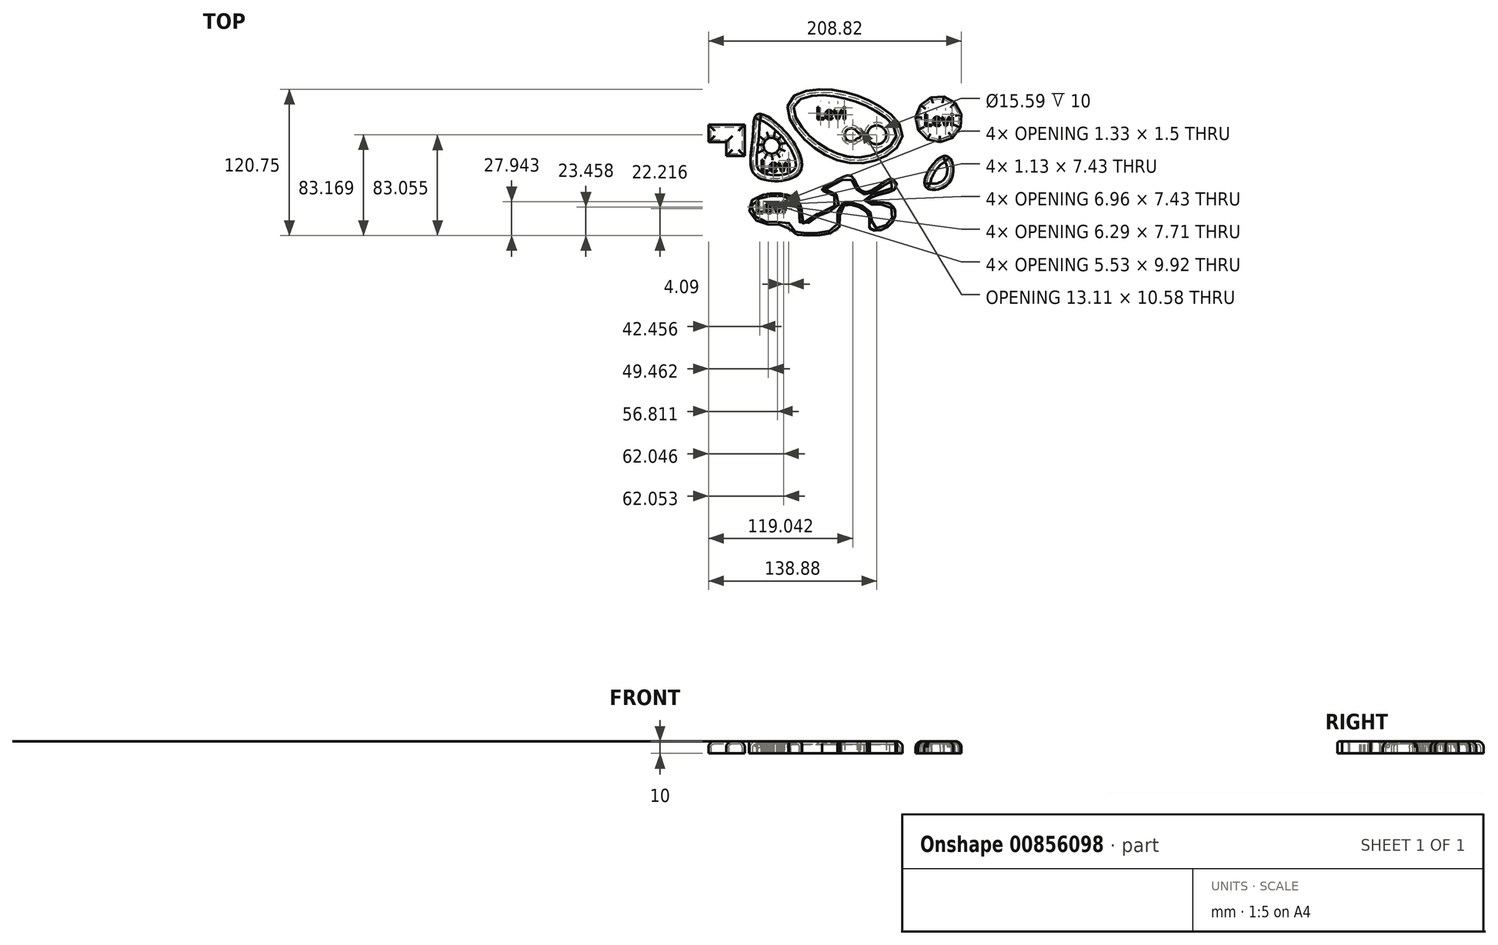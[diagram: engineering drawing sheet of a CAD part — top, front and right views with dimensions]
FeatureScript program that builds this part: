
annotation { "Feature Type Name" : "Feature", "Feature Type Description" : "" }
export const myFeature = defineFeature(function(context is Context, id is Id, definition is map)
    precondition{}
    {
        {
            var Q0;
            Q0=qCreatedBy(makeId("Top.planeOp"),FACE);
            var sketch = newSketch(context, id + "F0", { "sketchPlane" : qUnion([Q0])});
            skFitSpline(sketch, "E0", {"points": [v(-47.11, 34.08) * mm, v(1.5, -12.36) * mm, v(47.93, 10.45) * mm, v(-5.02, 46.84) * mm, v(-47.11, 34.08) * mm]});
            skFitSpline(sketch, "E1", {"points": [v(39.51, -25.93) * mm, v(20.23, -36.25) * mm, v(11, -32.45) * mm, v(5.02, -23.22) * mm, v(-9.37, -28.65) * mm, v(-18.33, -35.17) * mm, v(-6.38, -41.68) * mm, v(-9.64, -49.29) * mm, v(-23.49, -55.26) * mm, v(-34.62, -62.32) * mm, v(-38.42, -44.13) * mm, v(-76.98, -44.13) * mm, v(-70.2, -61.78) * mm, v(-46.3, -64.5) * mm, v(-45.48, -69.38) * mm, v(-10.73, -70.47) * mm, v(-3.67, -62.32) * mm, v(-1.5, -48.2) * mm, v(19.69, -54.99) * mm, v(21.05, -67.2) * mm, v(36.25, -65.04) * mm, v(41.68, -51.73) * mm, v(33.8, -45.48) * mm, v(18.6, -44.4) * mm, v(24.58, -40.05) * mm, v(42.77, -33) * mm, v(39.51, -25.93) * mm]});
            skFitSpline(sketch, "E2", {"points": [v(-75.9, 7.2) * mm, v(-73.18, -23.22) * mm, v(-37.88, -21.59) * mm, v(-47.66, 11.54) * mm, v(-72.1, 27.3) * mm, v(-75.9, 7.2) * mm]});
            skFitSpline(sketch, "E3", {"points": [v(83.23, -6.92) * mm, v(66.4, -31.36) * mm, v(87.03, -28.1) * mm, v(83.23, -6.92) * mm]});
            skCircle(sketch, "E4", {"center": v(5.57, 10.45) * mm, "radius": 5.44 * mm});
            skCircle(sketch, "E5", {"center": v(10.98, 9.91) * mm, "radius": 2.3 * mm});
            skCircle(sketch, "E6", {"center": v(26.55, 10.45) * mm, "radius": 7.8 * mm});
            skCircle(sketch, "E7.cCircle", {"center": v(-60.2, 1.5) * mm, "radius": 6.57 * mm, "construction": true});
            skLineSegment(sketch, "E7.0", {"start": v(-58.6, 8.15) * mm, "end": v(-55.26, 6.24) * mm});
            skLineSegment(sketch, "E7.1", {"start": v(-55.26, 6.24) * mm, "end": v(-53.48, 2.82) * mm});
            skLineSegment(sketch, "E7.2", {"start": v(-53.48, 2.82) * mm, "end": v(-53.83, -1.02) * mm});
            skLineSegment(sketch, "E7.3", {"start": v(-53.83, -1.02) * mm, "end": v(-56.2, -4.06) * mm});
            skLineSegment(sketch, "E7.4", {"start": v(-56.2, -4.06) * mm, "end": v(-59.84, -5.34) * mm});
            skLineSegment(sketch, "E7.5", {"start": v(-59.84, -5.34) * mm, "end": v(-63.59, -4.45) * mm});
            skLineSegment(sketch, "E7.6", {"start": v(-63.59, -4.45) * mm, "end": v(-66.26, -1.67) * mm});
            skLineSegment(sketch, "E7.7", {"start": v(-66.26, -1.67) * mm, "end": v(-67.01, 2.11) * mm});
            skLineSegment(sketch, "E7.8", {"start": v(-67.01, 2.11) * mm, "end": v(-65.6, 5.7) * mm});
            skLineSegment(sketch, "E7.9", {"start": v(-65.6, 5.7) * mm, "end": v(-62.46, 7.95) * mm});
            skLineSegment(sketch, "E7.10", {"start": v(-62.46, 7.95) * mm, "end": v(-58.6, 8.15) * mm});
            skPoint(sketch, "E7.0.midPoint", {"position": v(-56.93, 7.2) * mm});
            skCircle(sketch, "E8.cCircle", {"center": v(77.76, 23.49) * mm, "radius": 18.36 * mm, "construction": true});
            skLineSegment(sketch, "E8.0", {"start": v(82.01, 42.14) * mm, "end": v(91.42, 36.88) * mm});
            skLineSegment(sketch, "E8.1", {"start": v(91.42, 36.88) * mm, "end": v(96.5, 27.37) * mm});
            skLineSegment(sketch, "E8.2", {"start": v(96.5, 27.37) * mm, "end": v(95.61, 16.62) * mm});
            skLineSegment(sketch, "E8.3", {"start": v(95.61, 16.62) * mm, "end": v(89.06, 8.06) * mm});
            skLineSegment(sketch, "E8.4", {"start": v(89.06, 8.06) * mm, "end": v(78.93, 4.4) * mm});
            skLineSegment(sketch, "E8.5", {"start": v(78.93, 4.4) * mm, "end": v(68.42, 6.8) * mm});
            skLineSegment(sketch, "E8.6", {"start": v(68.42, 6.8) * mm, "end": v(60.87, 14.5) * mm});
            skLineSegment(sketch, "E8.7", {"start": v(60.87, 14.5) * mm, "end": v(58.69, 25.05) * mm});
            skLineSegment(sketch, "E8.8", {"start": v(58.69, 25.05) * mm, "end": v(62.56, 35.11) * mm});
            skLineSegment(sketch, "E8.9", {"start": v(62.56, 35.11) * mm, "end": v(71.25, 41.48) * mm});
            skLineSegment(sketch, "E8.10", {"start": v(71.25, 41.48) * mm, "end": v(82.01, 42.14) * mm});
            skPoint(sketch, "E8.0.midPoint", {"position": v(86.72, 39.51) * mm});
            skLineSegment(sketch, "E9.bottom", {"start": v(-112.33, 4.48) * mm, "end": v(-97.67, 4.48) * mm});
            skLineSegment(sketch, "E9.top", {"start": v(-112.33, 18.87) * mm, "end": v(-97.67, 18.87) * mm});
            skLineSegment(sketch, "E9.left", {"start": v(-112.33, 4.48) * mm, "end": v(-112.33, 18.87) * mm});
            skLineSegment(sketch, "E9.right", {"start": v(-97.67, 4.48) * mm, "end": v(-97.67, 18.87) * mm});
            skLineSegment(sketch, "E10.bottom", {"start": v(-97.67, 18.87) * mm, "end": v(-82.46, 18.87) * mm});
            skLineSegment(sketch, "E10.top", {"start": v(-97.67, -6.92) * mm, "end": v(-82.46, -6.92) * mm});
            skLineSegment(sketch, "E10.left", {"start": v(-97.67, 18.87) * mm, "end": v(-97.67, -6.92) * mm});
            skLineSegment(sketch, "E10.right", {"start": v(-82.46, 18.87) * mm, "end": v(-82.46, -6.92) * mm});
            skPoint(sketch, "E11", {"position": v(-26.25, 17.79) * mm});
            skSolve(sketch);
        }
        {
            var Q0;
            Q0 = qSketchRegion(id + "F0", true);
            extrude(context, id + "F1", {"entities" : qUnion([Q0]), "depth" : 10 * mm, "offsetDistance" : 25 * mm});
        }
        {
            var Q0;
            Q0=makeQuery(id+"F1.opExtrude","CAP_EDGE",EDGE,{"disambiguationData":[OSD([sQuery(id+"F0.wireOp",EDGE,"E9.top"),sQuery(id+"F0.wireOp",EDGE,"E10.bottom")])],"isStart":false});
            var Q1;
            Q1=makeQuery(id+"F1.opExtrude","CAP_EDGE",EDGE,{"disambiguationData":[OSD([sQuery(id+"F0.wireOp",EDGE,"E9.left")])],"isStart":false});
            var Q2;
            Q2=makeQuery(id+"F1.opExtrude","CAP_EDGE",EDGE,{"disambiguationData":[OSD([sQuery(id+"F0.wireOp",EDGE,"E9.bottom")])],"isStart":false});
            var Q3;
            Q3=makeQuery(id+"F1.opExtrude","CAP_EDGE",EDGE,{"disambiguationData":[OSD([sQuery(id+"F0.wireOp",EDGE,"E10.top")])],"isStart":false});
            var Q4;
            Q4=makeQuery(id+"F1.opExtrude","CAP_EDGE",EDGE,{"disambiguationData":[OSD([sQuery(id+"F0.wireOp",EDGE,"E10.left")])],"isStart":false});
            var Q5;
            Q5=makeQuery(id+"F1.opExtrude","CAP_EDGE",EDGE,{"disambiguationData":[OSD([sQuery(id+"F0.wireOp",EDGE,"E10.right")])],"isStart":false});
            var Q6;
            Q6=makeQuery(id+"F1.opExtrude","CAP_EDGE",EDGE,{"disambiguationData":[OSD([sQuery(id+"F0.wireOp",EDGE,"E0")])],"isStart":false});
            var Q7;
            Q7=makeQuery(id+"F1.opExtrude","CAP_FACE",FACE,{"disambiguationData":[OSD([sQuery(id+"F0.wireOp",EDGE,"E8.0"),sQuery(id+"F0.wireOp",EDGE,"E8.1"),sQuery(id+"F0.wireOp",EDGE,"E8.2"),sQuery(id+"F0.wireOp",EDGE,"E8.3"),sQuery(id+"F0.wireOp",EDGE,"E8.4"),sQuery(id+"F0.wireOp",EDGE,"E8.5"),sQuery(id+"F0.wireOp",EDGE,"E8.6"),sQuery(id+"F0.wireOp",EDGE,"E8.7"),sQuery(id+"F0.wireOp",EDGE,"E8.8"),sQuery(id+"F0.wireOp",EDGE,"E8.9"),sQuery(id+"F0.wireOp",EDGE,"E8.10")])],"isStart":false});
            var Q8;
            Q8=makeQuery(id+"F1.opExtrude","CAP_EDGE",EDGE,{"disambiguationData":[OSD([sQuery(id+"F0.wireOp",EDGE,"E3")])],"isStart":false});
            var Q9;
            Q9=makeQuery(id+"F1.opExtrude","CAP_FACE",FACE,{"disambiguationData":[OSD([sQuery(id+"F0.wireOp",EDGE,"E2"),sQuery(id+"F0.wireOp",EDGE,"E7.0"),sQuery(id+"F0.wireOp",EDGE,"E7.1"),sQuery(id+"F0.wireOp",EDGE,"E7.2"),sQuery(id+"F0.wireOp",EDGE,"E7.3"),sQuery(id+"F0.wireOp",EDGE,"E7.4"),sQuery(id+"F0.wireOp",EDGE,"E7.5"),sQuery(id+"F0.wireOp",EDGE,"E7.6"),sQuery(id+"F0.wireOp",EDGE,"E7.7"),sQuery(id+"F0.wireOp",EDGE,"E7.8"),sQuery(id+"F0.wireOp",EDGE,"E7.9"),sQuery(id+"F0.wireOp",EDGE,"E7.10")])],"isStart":false});
            fillet(context, id + "F2", {"entities" : qUnion([Q0, Q1, Q2, Q3, Q4, Q5, Q6, Q7, Q8, Q9]), "radius" : 5 * mm, "tangentPropagation" : true, "allowEdgeOverflow" : false});
        }
        {
            var Q0;
            Q0=makeQuery(id+"F1.opExtrude","CAP_EDGE",EDGE,{"disambiguationData":[OSD([sQuery(id+"F0.wireOp",EDGE,"E1")])],"isStart":false});
            fillet(context, id + "F3", {"entities" : qUnion([Q0]), "radius" : 2 * mm, "tangentPropagation" : true, "allowEdgeOverflow" : false});
        }
        {
            var Q0;
            Q0=makeQuery(id+"F1.opExtrude","CAP_FACE",FACE,{"disambiguationData":[OSD([sQuery(id+"F0.wireOp",EDGE,"E0"),sQuery(id+"F0.wireOp",EDGE,"E4"),sQuery(id+"F0.wireOp",EDGE,"E5"),sQuery(id+"F0.wireOp",EDGE,"E6")])],"isStart":true});
            shell(context, id + "F4", {"entities" : qUnion([Q0]), "thickness" : 2.5 * mm});
        }
        {
            var Q0;
            Q0=makeQuery(id+"F1.opExtrude","CAP_FACE",FACE,{"disambiguationData":[OSD([sQuery(id+"F0.wireOp",EDGE,"E2"),sQuery(id+"F0.wireOp",EDGE,"E7.0"),sQuery(id+"F0.wireOp",EDGE,"E7.1"),sQuery(id+"F0.wireOp",EDGE,"E7.2"),sQuery(id+"F0.wireOp",EDGE,"E7.3"),sQuery(id+"F0.wireOp",EDGE,"E7.4"),sQuery(id+"F0.wireOp",EDGE,"E7.5"),sQuery(id+"F0.wireOp",EDGE,"E7.6"),sQuery(id+"F0.wireOp",EDGE,"E7.7"),sQuery(id+"F0.wireOp",EDGE,"E7.8"),sQuery(id+"F0.wireOp",EDGE,"E7.9"),sQuery(id+"F0.wireOp",EDGE,"E7.10")])],"isStart":true});
            var Q1;
            Q1=makeQuery(id+"F1.opExtrude","CAP_FACE",FACE,{"disambiguationData":[OSD([sQuery(id+"F0.wireOp",EDGE,"E9.bottom"),sQuery(id+"F0.wireOp",EDGE,"E9.top"),sQuery(id+"F0.wireOp",EDGE,"E9.left"),sQuery(id+"F0.wireOp",EDGE,"E10.bottom"),sQuery(id+"F0.wireOp",EDGE,"E10.top"),sQuery(id+"F0.wireOp",EDGE,"E10.left"),sQuery(id+"F0.wireOp",EDGE,"E10.right")])],"isStart":true});
            var Q2;
            Q2=makeQuery(id+"F1.opExtrude","CAP_FACE",FACE,{"disambiguationData":[OSD([sQuery(id+"F0.wireOp",EDGE,"E3")])],"isStart":true});
            var Q3;
            Q3=makeQuery(id+"F1.opExtrude","CAP_FACE",FACE,{"disambiguationData":[OSD([sQuery(id+"F0.wireOp",EDGE,"E8.0"),sQuery(id+"F0.wireOp",EDGE,"E8.1"),sQuery(id+"F0.wireOp",EDGE,"E8.2"),sQuery(id+"F0.wireOp",EDGE,"E8.3"),sQuery(id+"F0.wireOp",EDGE,"E8.4"),sQuery(id+"F0.wireOp",EDGE,"E8.5"),sQuery(id+"F0.wireOp",EDGE,"E8.6"),sQuery(id+"F0.wireOp",EDGE,"E8.7"),sQuery(id+"F0.wireOp",EDGE,"E8.8"),sQuery(id+"F0.wireOp",EDGE,"E8.9"),sQuery(id+"F0.wireOp",EDGE,"E8.10")])],"isStart":true});
            shell(context, id + "F5", {"entities" : qUnion([Q0, Q1, Q2, Q3]), "thickness" : 2 * mm});
        }
        {
            var Q0;
            Q0=makeQuery(id+"F1.opExtrude","CAP_FACE",FACE,{"disambiguationData":[OSD([sQuery(id+"F0.wireOp",EDGE,"E1")])],"isStart":false});
            var sketch = newSketch(context, id + "F6", { "sketchPlane" : qUnion([Q0])});
            skText(sketch, "E12", { "text": "Levi", "fontName": "OpenSans-Regular.ttf"});
            skText(sketch, "E13", { "text": "Levi", "fontName": "OpenSans-Regular.ttf"});
            skText(sketch, "E14", { "text": "Levi", "fontName": "OpenSans-Regular.ttf"});
            skText(sketch, "E15", { "text": "Levi", "fontName": "OpenSans-Regular.ttf"});
            const initialGuessF6  = {"E12": [-0.074, -0.0541, 1, 0, 0.01], "E13": [-0.0239, 0.02336, 1, 0, 0.01], "E14": [0.06502, 0.01785, 1, 0, 0.01], "E15": [-0.06991, -0.02003, 1, 0, 0.01]};
            skSetInitialGuess(sketch, initialGuessF6);
            skSolve(sketch);
        }
        {
            var Q0;
            Q0 = qSketchRegion(id + "F6", true);
            extrude(context, id + "F7", {"entities" : qUnion([Q0]), "operationType" : NewBodyOperationType.REMOVE, "oppositeDirection" : true, "depth" : 12 * mm, "offsetDistance" : 25 * mm});
        }
    });
